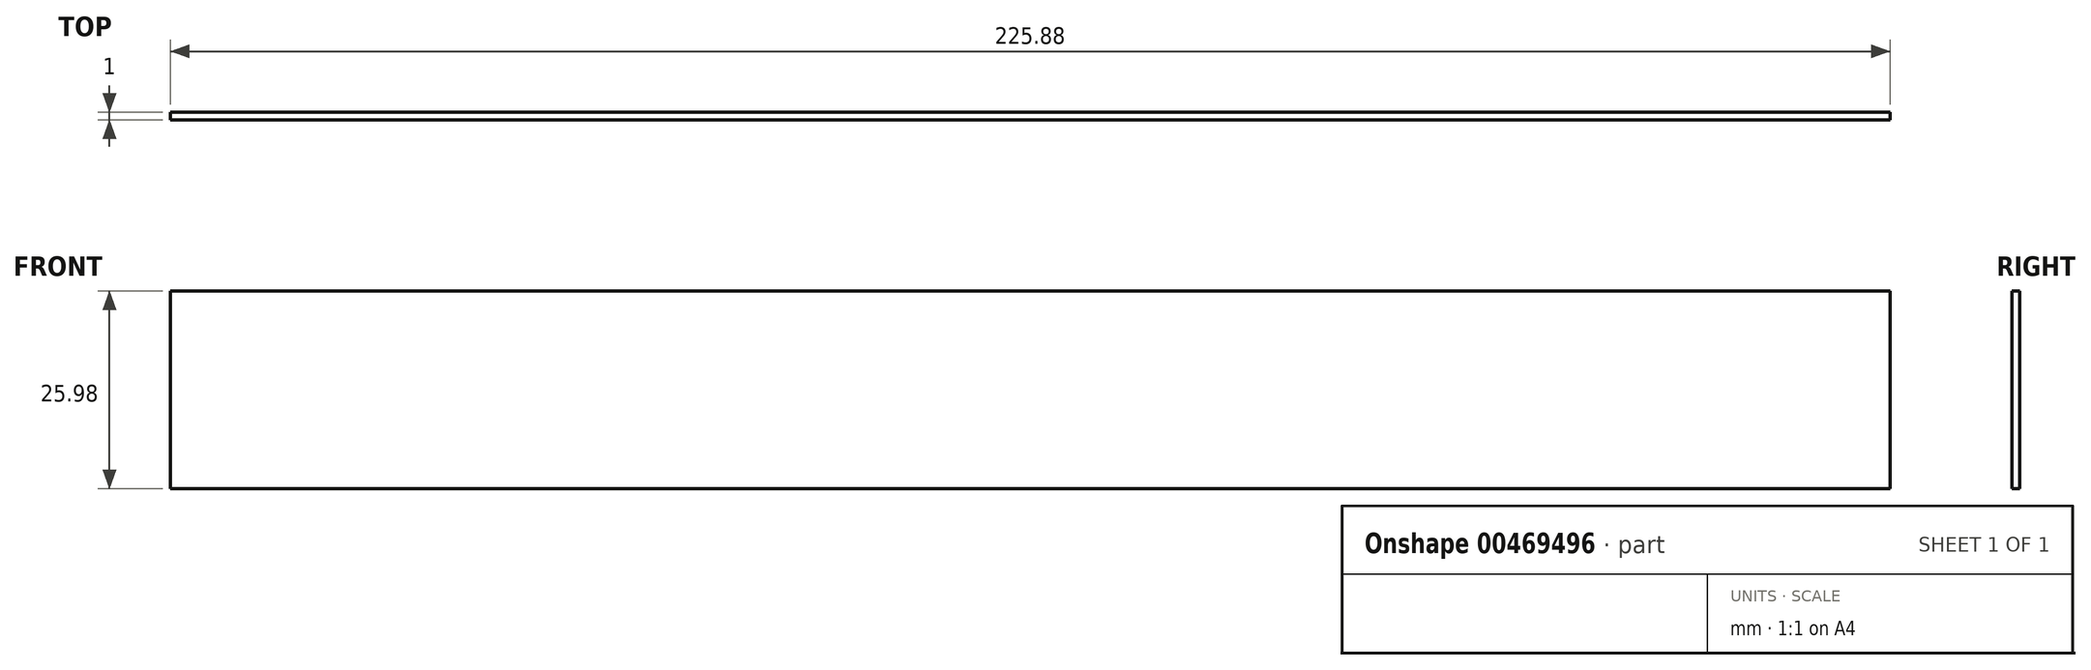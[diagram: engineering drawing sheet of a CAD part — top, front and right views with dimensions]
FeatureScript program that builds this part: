
annotation { "Feature Type Name" : "Feature", "Feature Type Description" : "" }
export const myFeature = defineFeature(function(context is Context, id is Id, definition is map)
    precondition{}
    {
        {
            var Q0;
            Q0=qCreatedBy(makeId("Front.planeOp"),FACE);
            var sketch = newSketch(context, id + "F0", { "sketchPlane" : qUnion([Q0])});
            skLineSegment(sketch, "E0.bottom", {"start": v(112.94, 13) * mm, "end": v(-112.94, 13) * mm});
            skLineSegment(sketch, "E0.top", {"start": v(112.94, -13) * mm, "end": v(-112.94, -13) * mm});
            skLineSegment(sketch, "E0.left", {"start": v(112.94, 13) * mm, "end": v(112.94, -13) * mm});
            skLineSegment(sketch, "E0.right", {"start": v(-112.94, 13) * mm, "end": v(-112.94, -13) * mm});
            skPoint(sketch, "E0.middle", {"position": v(0, 0) * mm});
            skSolve(sketch);
        }
        {
            var Q0;
            Q0=makeQuery(id+"F0.imprint","IMPRINT",FACE,{"disambiguationData":[TD([[makeQuery(id+"F0.imprint","IMPRINT",EDGE,{"derivedFrom":sQuery(id+"F0.wireOp",EDGE,"E0.bottom")}),1.0]])]});
            extrude(context, id + "F1", {"entities" : qUnion([Q0]), "depth" : 1 * mm});
        }
    });
